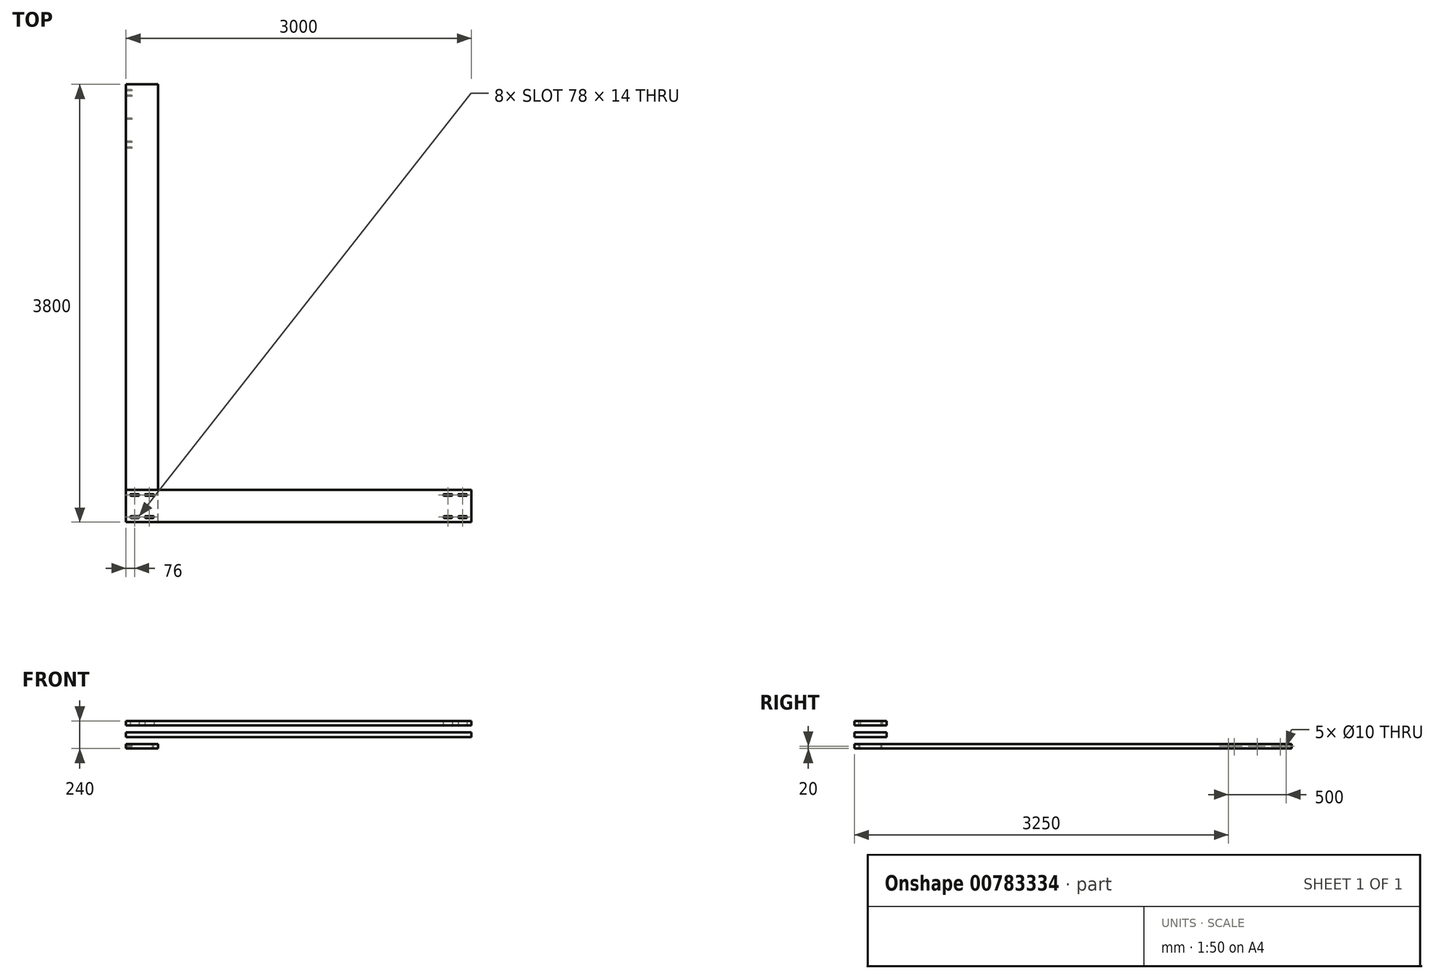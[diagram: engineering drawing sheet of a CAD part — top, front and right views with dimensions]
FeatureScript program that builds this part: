
annotation { "Feature Type Name" : "Feature", "Feature Type Description" : "" }
export const myFeature = defineFeature(function(context is Context, id is Id, definition is map)
    precondition{}
    {
        {
            var Q0;
            Q0=qCreatedBy(makeId("Top.planeOp"),FACE);
            var sketch = newSketch(context, id + "F0", { "sketchPlane" : qUnion([Q0])});
            skLineSegment(sketch, "E0.bottom", {"start": v(280, 0) * mm, "end": v(0, 0) * mm});
            skLineSegment(sketch, "E0.top", {"start": v(280, 3800) * mm, "end": v(0, 3800) * mm});
            skLineSegment(sketch, "E0.left", {"start": v(280, 0) * mm, "end": v(280, 3800) * mm});
            skLineSegment(sketch, "E0.right", {"start": v(0, 0) * mm, "end": v(0, 3800) * mm});
            skSolve(sketch);
        }
        {
            var Q0;
            Q0 = qSketchRegion(id + "F0", true);
            extrude(context, id + "F1", {"entities" : qUnion([Q0]), "depth" : 40 * mm, "offsetDistance" : 25 * mm});
        }
        {
            var Q0;
            Q0=qCreatedBy(makeId("Top.planeOp"),FACE);
            cPlane(context, id + "F2", {"entities" : qUnion([Q0]), "cplaneType" : CPlaneType.OFFSET, "offset" : 100 * mm, "width" : 150 * mm, "height" : 150 * mm});
        }
        {
            var Q0;
            Q0=qCreatedBy(id+"F2.planeOp",FACE);
            var sketch = newSketch(context, id + "F3", { "sketchPlane" : qUnion([Q0])});
            skLineSegment(sketch, "E1.bottom", {"start": v(0, 0) * mm, "end": v(3000, 0) * mm});
            skLineSegment(sketch, "E1.top", {"start": v(0, 280) * mm, "end": v(3000, 280) * mm});
            skLineSegment(sketch, "E1.left", {"start": v(0, 0) * mm, "end": v(0, 280) * mm});
            skLineSegment(sketch, "E1.right", {"start": v(3000, 0) * mm, "end": v(3000, 280) * mm});
            skSolve(sketch);
        }
        {
            var Q0;
            Q0 = qSketchRegion(id + "F3", true);
            extrude(context, id + "F4", {"entities" : qUnion([Q0]), "depth" : 40 * mm, "offsetDistance" : 25 * mm});
        }
        {
            var Q0;
            Q0=qCreatedBy(id+"F2.planeOp",FACE);
            cPlane(context, id + "F5", {"entities" : qUnion([Q0]), "cplaneType" : CPlaneType.OFFSET, "offset" : 100 * mm, "width" : 150 * mm, "height" : 150 * mm});
        }
        {
            var Q0;
            Q0=qCreatedBy(id+"F5.planeOp",FACE);
            var sketch = newSketch(context, id + "F6", { "sketchPlane" : qUnion([Q0])});
            skLineSegment(sketch, "E2.bottom", {"start": v(0, 0) * mm, "end": v(3000, 0) * mm});
            skLineSegment(sketch, "E2.top", {"start": v(0, 280) * mm, "end": v(3000, 280) * mm});
            skLineSegment(sketch, "E2.left", {"start": v(0, 0) * mm, "end": v(0, 280) * mm});
            skLineSegment(sketch, "E2.right", {"start": v(3000, 0) * mm, "end": v(3000, 280) * mm});
            skLineSegment(sketch, "E3", {"start": v(44, 51) * mm, "end": v(108, 51) * mm});
            skArc(sketch, "E4", {"start": v(108, 37) * mm, "mid": v(115, 44) * mm, "end": v(108, 51) * mm});
            skLineSegment(sketch, "E5", {"start": v(108, 37) * mm, "end": v(44, 37) * mm});
            skArc(sketch, "E6", {"start": v(44, 51) * mm, "mid": v(37, 44) * mm, "end": v(44, 37) * mm});
            skLineSegment(sketch, "E7", {"start": v(3000, 140) * mm, "end": v(0, 140) * mm, "construction": true});
            skLineSegment(sketch, "E8", {"start": v(1500, 0) * mm, "end": v(1500, 280) * mm, "construction": true});
            skLineSegment(sketch, "E9.bottom", {"start": v(15, 265) * mm, "end": v(265, 265) * mm, "construction": true});
            skLineSegment(sketch, "E9.top", {"start": v(15, 15) * mm, "end": v(265, 15) * mm, "construction": true});
            skLineSegment(sketch, "E9.left", {"start": v(15, 265) * mm, "end": v(15, 15) * mm, "construction": true});
            skLineSegment(sketch, "E9.right", {"start": v(265, 265) * mm, "end": v(265, 15) * mm, "construction": true});
            skLineSegment(sketch, "E10", {"start": v(140, 265) * mm, "end": v(140, 280) * mm, "construction": true});
            skLineSegment(sketch, "E11", {"start": v(140, 15) * mm, "end": v(140, 0) * mm, "construction": true});
            skLineSegment(sketch, "E12", {"start": v(0, 140) * mm, "end": v(15, 140) * mm, "construction": true});
            skLineSegment(sketch, "E13.MirrorCS", {"start": v(172, 37) * mm, "end": v(236, 37) * mm});
            skLineSegment(sketch, "E14.MirrorCS", {"start": v(236, 51) * mm, "end": v(172, 51) * mm});
            skArc(sketch, "E15.MirrorCS", {"start": v(236, 51) * mm, "mid": v(243, 44) * mm, "end": v(236, 37) * mm});
            skArc(sketch, "E16.MirrorCS", {"start": v(172, 37) * mm, "mid": v(165, 44) * mm, "end": v(172, 51) * mm});
            skLineSegment(sketch, "E17.MirrorCS", {"start": v(236, 229) * mm, "end": v(172, 229) * mm});
            skArc(sketch, "E18.MirrorCS", {"start": v(172, 243) * mm, "mid": v(165, 236) * mm, "end": v(172, 229) * mm});
            skLineSegment(sketch, "E19.MirrorCS", {"start": v(172, 243) * mm, "end": v(236, 243) * mm});
            skArc(sketch, "E20.MirrorCS", {"start": v(236, 229) * mm, "mid": v(243, 236) * mm, "end": v(236, 243) * mm});
            skLineSegment(sketch, "E21.MirrorCS", {"start": v(44, 229) * mm, "end": v(108, 229) * mm});
            skLineSegment(sketch, "E22.MirrorCS", {"start": v(108, 243) * mm, "end": v(44, 243) * mm});
            skArc(sketch, "E23.MirrorCS", {"start": v(108, 243) * mm, "mid": v(115, 236) * mm, "end": v(108, 229) * mm});
            skArc(sketch, "E24.MirrorCS", {"start": v(44, 229) * mm, "mid": v(37, 236) * mm, "end": v(44, 243) * mm});
            skArc(sketch, "E25.MirrorCS", {"start": v(2956, 51) * mm, "mid": v(2963, 44) * mm, "end": v(2956, 37) * mm});
            skLineSegment(sketch, "E26.MirrorCS", {"start": v(2956, 51) * mm, "end": v(2892, 51) * mm});
            skArc(sketch, "E27.MirrorCS", {"start": v(2892, 37) * mm, "mid": v(2885, 44) * mm, "end": v(2892, 51) * mm});
            skLineSegment(sketch, "E28.MirrorCS", {"start": v(2892, 37) * mm, "end": v(2956, 37) * mm});
            skArc(sketch, "E29.MirrorCS", {"start": v(2828, 37) * mm, "mid": v(2835, 44) * mm, "end": v(2828, 51) * mm});
            skLineSegment(sketch, "E30.MirrorCS", {"start": v(2764, 51) * mm, "end": v(2828, 51) * mm});
            skLineSegment(sketch, "E31.MirrorCS", {"start": v(2828, 37) * mm, "end": v(2764, 37) * mm});
            skArc(sketch, "E32.MirrorCS", {"start": v(2764, 51) * mm, "mid": v(2757, 44) * mm, "end": v(2764, 37) * mm});
            skLineSegment(sketch, "E33.MirrorCS", {"start": v(2764, 229) * mm, "end": v(2828, 229) * mm});
            skArc(sketch, "E34.MirrorCS", {"start": v(2828, 243) * mm, "mid": v(2835, 236) * mm, "end": v(2828, 229) * mm});
            skLineSegment(sketch, "E35.MirrorCS", {"start": v(2828, 243) * mm, "end": v(2764, 243) * mm});
            skArc(sketch, "E36.MirrorCS", {"start": v(2764, 229) * mm, "mid": v(2757, 236) * mm, "end": v(2764, 243) * mm});
            skArc(sketch, "E37.MirrorCS", {"start": v(2892, 243) * mm, "mid": v(2885, 236) * mm, "end": v(2892, 229) * mm});
            skLineSegment(sketch, "E38.MirrorCS", {"start": v(2892, 243) * mm, "end": v(2956, 243) * mm});
            skLineSegment(sketch, "E39.MirrorCS", {"start": v(2956, 229) * mm, "end": v(2892, 229) * mm});
            skArc(sketch, "E40.MirrorCS", {"start": v(2956, 229) * mm, "mid": v(2963, 236) * mm, "end": v(2956, 243) * mm});
            skSolve(sketch);
        }
        {
            var Q0;
            Q0 = qSketchRegion(id + "F6", true);
            extrude(context, id + "F7", {"entities" : qUnion([Q0]), "depth" : 40 * mm, "offsetDistance" : 25 * mm});
        }
        {
            var Q0;
            Q0=sQuery(id+"F6.wireOp",VERTEX,"E24.MirrorCS.center");
            var Q1;
            Q1=sQuery(id+"F6.wireOp",VERTEX,"E20.MirrorCS.center");
            var Q2;
            Q2=sQuery(id+"F6.wireOp",VERTEX,"E15.MirrorCS.center");
            var Q3;
            Q3=sQuery(id+"F6.wireOp",VERTEX,"E6.center");
            var Q4;
            Q4=makeQuery(id+"F1.opExtrude","SWEPT_BODY",BODY,{"disambiguationData":[OSD([sQuery(id+"F0.wireOp",EDGE,"E0.bottom"),sQuery(id+"F0.wireOp",EDGE,"E0.top"),sQuery(id+"F0.wireOp",EDGE,"E0.left"),sQuery(id+"F0.wireOp",EDGE,"E0.right")])]});
            hole(context, id + "F8", {"style" : HoleStyle.C_SINK, "endStyle" : HoleEndStyle.THROUGH, "holeDiameter" : 8 * mm, "cSinkDiameter" : 15 * mm, "cSinkAngle" : 90 * degree, "majorDiameter" : 5 * mm, "isTappedThrough" : true, "tappedDepth" : 12 * mm, "tapClearance" : 3, "locations" : qUnion([Q0, Q1, Q2, Q3]), "scope" : qUnion([Q4])});
        }
        {
            var Q0;
            Q0=makeQuery(id+"F1.opExtrude","SWEPT_FACE",FACE,{"disambiguationData":[OSD([sQuery(id+"F0.wireOp",EDGE,"E0.right")])]});
            var sketch = newSketch(context, id + "F9", { "sketchPlane" : qUnion([Q0])});
            skLineSegment(sketch, "E41", {"start": v(-3800, 20) * mm, "end": v(-3750, 20) * mm, "construction": true});
            skLineSegment(sketch, "E42", {"start": v(-3750, 20) * mm, "end": v(-3700, 20) * mm, "construction": true});
            skLineSegment(sketch, "E43", {"start": v(-3700, 20) * mm, "end": v(-3500, 20) * mm, "construction": true});
            skLineSegment(sketch, "E44", {"start": v(-3500, 20) * mm, "end": v(-3300, 20) * mm, "construction": true});
            skLineSegment(sketch, "E45", {"start": v(-3300, 20) * mm, "end": v(-3250, 20) * mm, "construction": true});
            skLineSegment(sketch, "E46", {"start": v(-3250, 20) * mm, "end": v(-3200, 20) * mm, "construction": true});
            skLineSegment(sketch, "E47", {"start": v(-3200, 40) * mm, "end": v(-3200, 0) * mm, "construction": true});
            skSolve(sketch);
        }
        {
            var Q0;
            Q0=sQuery(id+"F9.wireOp",VERTEX,"E41.end");
            var Q1;
            Q1=sQuery(id+"F9.wireOp",VERTEX,"E42.end");
            var Q2;
            Q2=sQuery(id+"F9.wireOp",VERTEX,"E43.end");
            var Q3;
            Q3=sQuery(id+"F9.wireOp",VERTEX,"E44.end");
            var Q4;
            Q4=sQuery(id+"F9.wireOp",VERTEX,"E45.end");
            var Q5;
            Q5=makeQuery(id+"F1.opExtrude","SWEPT_BODY",BODY,{"disambiguationData":[OSD([sQuery(id+"F0.wireOp",EDGE,"E0.bottom"),sQuery(id+"F0.wireOp",EDGE,"E0.top"),sQuery(id+"F0.wireOp",EDGE,"E0.left"),sQuery(id+"F0.wireOp",EDGE,"E0.right")])]});
            hole(context, id + "F10", {"style" : HoleStyle.C_SINK, "endStyle" : HoleEndStyle.BLIND, "holeDiameter" : 10 * mm, "cSinkDiameter" : 16 * mm, "cSinkAngle" : 90 * degree, "majorDiameter" : 5 * mm, "holeDepth" : 50 * mm, "isTappedThrough" : true, "tappedDepth" : 12 * mm, "tapClearance" : 3, "locations" : qUnion([Q0, Q1, Q2, Q3, Q4]), "scope" : qUnion([Q5])});
        }
    });
